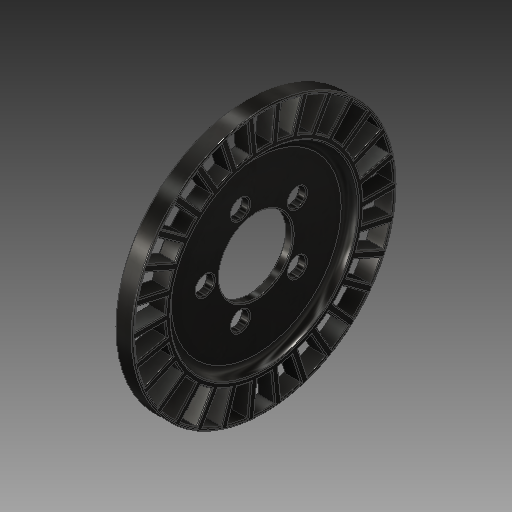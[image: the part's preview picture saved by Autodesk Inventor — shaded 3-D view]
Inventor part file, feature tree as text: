
AUTODESK INVENTOR PART (.ipt)
format: ipt  version: 2019 (Build 230136000, 136)  size: 1,476,608 bytes
history: native  units: mm
features: extrude x5, sketch x5, fillet x2, pattern_circular x2, plane x1, other x1
ambient origin geometry x8: Origin, YZ Plane, XZ Plane, XY Plane, X Axis, Y Axis, Z Axis, Center Point
bodies: Solid1 (feature_tree)
feature tree (16):
  extrude  "Extrusion1"  Depth=166.0mm
  extrude  "Extrusion2"  Depth=0.5mm
  fillet  "Fillet1"  Radius=0.5mm
  plane  "Work Plane1"
  extrude  "Extrusion3"  Depth=228.0mm
  extrude  "Extrusion4"  Depth=6.0mm
  pattern_circular  "Circular Pattern1"  [2 undecoded]
  extrude  "Extrusion5"  Depth=1.0mm TaperAngle=360.0deg
  pattern_circular  "Circular Pattern2"  Count=9  [1 undecoded]
  other  "Rule Fillet3"
  fillet  "Fillet2"  Radius=16.0mm
  sketch  "Sketch1"  dims[d14=15.0mm d15=0.0mm d16=166.0mm]
  sketch  "Sketch2"  dims[d17=7.5mm d18=0.0mm d19=8.0mm d20=0.5mm]
  sketch  "Sketch3"  dims[d21=234.0mm d22=228.0mm]
  sketch  "Sketch4"  dims[d23=15.5mm d24=0.0mm d25=6.0mm]
  sketch  "Sketch5"  dims[d26=28.0mm d27=0.0mm d28=0.0mm d29=300.0mm d30=360.0deg d34=90.0mm d38=16.0mm d39=10.0mm d40=0.0mm d41=50.0mm d42=360.0deg d44=1.0mm d45=1.0mm d51=65.0mm d57=175.45mm]
note: 3 required parameter values undecoded (feature->parameter linkage not recoverable at this tier; creation-order binding heuristic only, values carry confidence <= 0.55)
